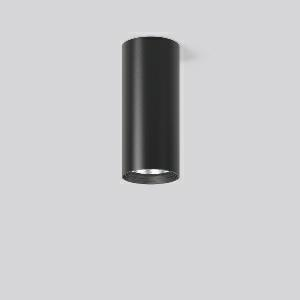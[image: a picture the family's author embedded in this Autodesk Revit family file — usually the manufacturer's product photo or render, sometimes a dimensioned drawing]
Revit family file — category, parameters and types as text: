
# Revit family: heledon_mini_a_931200_003_4768
name_source: partatom
category: Lighting Fixtures
units: mm (PartAtom-declared; Revit-internal decimal feet)

## family parameters
Cut with Voids When Loaded = No
Host = Face
Light Source = No
Part Type = Normal
Room Calculation Point = No
Round Connector Dimension = Use Diameter
Shared = No

## types (1)
- HELEDON mini A (1 x LED Modul 930, 2500 lm, 3000)
    Apparent Load = 20 VA
    Approval mark = CE
    CIE Flux Codes = 100 100 100 100 100
    Color Rendering = 90
    Color Temperature = 3000
    Default Elevation = 1800 mm
    Description = Series: HELEDON mini
Cylindrical surface-mounted downlight. Housing: die-cast aluminium, powder-coated. Internal ceiling frame polycarbonate with bayonet mounting. Black plastic ring and recessed LED to prevent glare from the side. Optical assembly with reflector made of MIRO-Silver with 98% total light reflection for outstanding efficiency - can be changed without tools. Best colour rendering index Ra>90. Suitable for Ceiling mounting. Easy installation with a separate ceiling frame with bayonet mounting and plug connection. Driver integrated. Connected via plug-in connector. High quality converter without flickering and stroboscopic effect. The following accessories can be mounted without use of tools: interchangeable lenses, decorative glasses, honeycomb louvre, clear and frosted diffusers, white interchangeable plastic ring. 
Colour: deep black, matt (RAL 9005)
Diameter: 87 mm
Height: 197 mm
Lamp: LED
Socket: without socket
Colour temperature: 3000K
Colour rendering index (CRI): 92
System power: 20 W
Rated luminous flux: 2500 lm
Luminous efficiency: 125 lm/W
Control gear: Regulated power supply
Protection class: I
Type of protection: IP 20
    Height = 197 mm
    Lamp = 1 x LED Modul 930
    Lamp Light Flux = 2500 lm
    Lamp count = 1
    Length = 87 mm
    Lifetime = 50000 h
    Luminous efficacy = 125 lm/W
    Manufacturer = RZB
    ModVariant = No
    Model = 931200.003
    Mounting Place = Ceiling
    Mounting Type = Surface mounted
    Number of Poles = 1
    OnlyDefault = Yes
    Power Factor = 1
    Product Name = HELEDON mini A
    Product group = Surface mounted downlights
    ProductGroupID = 302
    Protection Class = Protection class I
    Protection Degree = IP 20
    RLX_Detail_Level = 1
    RLX_Emergency_Light_Flux = 0 lm
    RLX_Emergency_Type = 0
    RLX_Emergency_Type_DB = No
    RlxData = <blob elided: 106249 chars, md5=42117556>
    Socket = socket
    Standby Power = 0 W
    System Light Flux = 2500 lm
    System Power = 20 W
    Type Comments = Product without accessories
    Type Image = 931188.003.jpg
    URL = http://relux.com
    VarID = ---
    Voltage = 230 V
    Voltage Range = 220-240 V
    Weight = 0.00 kg
    Width = 0 mm  [stored 0 ft]

note: [stored X ft] marks values corroborated as IEEE doubles in the binary element streams (Revit-internal decimal feet)

## geometry (parser evidence)
native form markers: Blend x4, Sweep x9
no freeform markers — native parametric forms only
